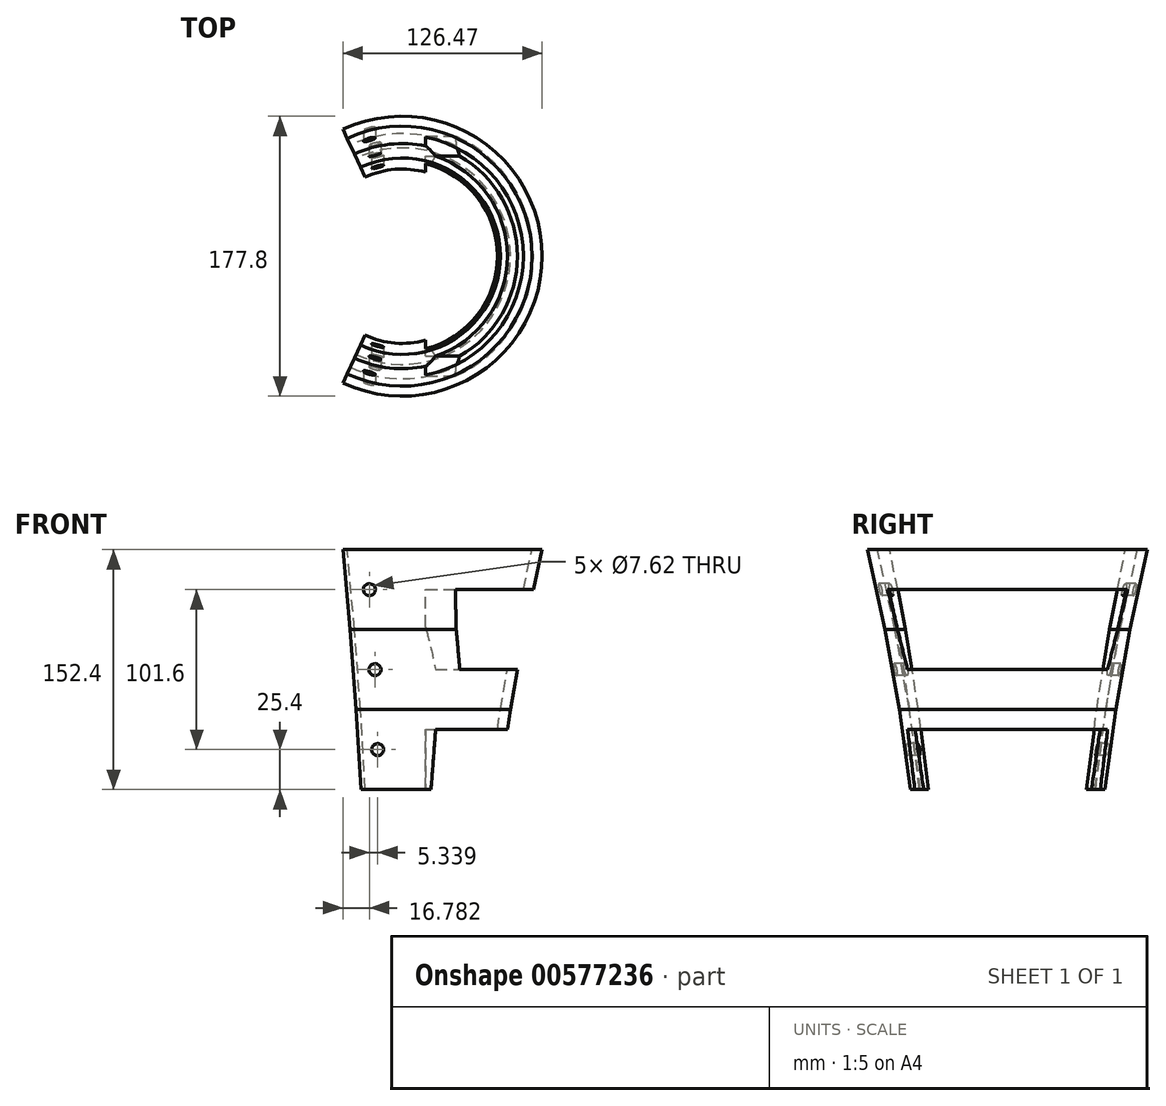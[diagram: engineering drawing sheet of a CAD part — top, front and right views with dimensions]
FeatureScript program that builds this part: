
annotation { "Feature Type Name" : "Feature", "Feature Type Description" : "" }
export const myFeature = defineFeature(function(context is Context, id is Id, definition is map)
    precondition{}
    {
        {
            var Q0;
            Q0=qCreatedBy(makeId("Front.planeOp"),FACE);
            var sketch = newSketch(context, id + "F0", { "sketchPlane" : qUnion([Q0])});
            skLineSegment(sketch, "E0", {"start": v(0, 0) * mm, "end": v(0, 50.8) * mm});
            skLineSegment(sketch, "E1", {"start": v(0, 50.8) * mm, "end": v(68.76, 50.8) * mm, "construction": true});
            skLineSegment(sketch, "E2", {"start": v(0, 0) * mm, "end": v(61.72, 0) * mm});
            skLineSegment(sketch, "E3", {"start": v(61.72, 0) * mm, "end": v(68.76, 50.8) * mm});
            skLineSegment(sketch, "E4", {"start": v(0, 50.8) * mm, "end": v(0, 101.6) * mm});
            skLineSegment(sketch, "E5", {"start": v(0, 101.6) * mm, "end": v(77.84, 101.6) * mm, "construction": true});
            skLineSegment(sketch, "E6", {"start": v(77.84, 101.6) * mm, "end": v(68.76, 50.8) * mm});
            skLineSegment(sketch, "E7", {"start": v(0, 101.6) * mm, "end": v(0, 152.4) * mm});
            skLineSegment(sketch, "E8", {"start": v(0, 152.4) * mm, "end": v(88.9, 152.4) * mm});
            skLineSegment(sketch, "E9", {"start": v(88.9, 152.4) * mm, "end": v(77.84, 101.6) * mm});
            skSolve(sketch);
        }
        {
            var Q0;
            Q0=qSketchRegion(id+"F0",true);
            var Q1;
            Q1=sQuery(id+"F0.wireOp",EDGE,"E7");
            revolve(context, id + "F1", {"entities" : qUnion([Q0]), "axis" : qUnion([Q1]), "revolveType" : RevolveType.SYMMETRIC, "angle" : 230 * degree});
        }
        {
            var Q0;
            Q0=qCreatedBy(makeId("Front.planeOp"),FACE);
            var sketch = newSketch(context, id + "F2", { "sketchPlane" : qUnion([Q0])});
            skLineSegment(sketch, "E10", {"start": v(0, 50.8) * mm, "end": v(62.4, 50.8) * mm, "construction": true});
            skLineSegment(sketch, "E11", {"start": v(0, 50.8) * mm, "end": v(0, 101.6) * mm});
            skLineSegment(sketch, "E12", {"start": v(0, 101.6) * mm, "end": v(71.49, 101.6) * mm, "construction": true});
            skLineSegment(sketch, "E13", {"start": v(71.49, 101.6) * mm, "end": v(62.4, 50.8) * mm});
            skLineSegment(sketch, "E14", {"start": v(0, 101.6) * mm, "end": v(0, 152.4) * mm});
            skLineSegment(sketch, "E15", {"start": v(0, 152.4) * mm, "end": v(82.55, 152.4) * mm});
            skLineSegment(sketch, "E16", {"start": v(82.55, 152.4) * mm, "end": v(71.49, 101.6) * mm});
            skPoint(sketch, "E17.start.orphan", {"position": v(1.44, 0) * mm});
            skLineSegment(sketch, "E18", {"start": v(0, 50.8) * mm, "end": v(0, 0) * mm});
            skLineSegment(sketch, "E19", {"start": v(0, 0) * mm, "end": v(55.37, 0) * mm});
            skLineSegment(sketch, "E20", {"start": v(55.37, 0) * mm, "end": v(62.4, 50.8) * mm});
            skSolve(sketch);
        }
        {
            var Q0;
            Q0=makeQuery(id+"F0.imprint","IMPRINT",FACE,{"disambiguationData":[TD([[makeQuery(id+"F0.imprint","IMPRINT",EDGE,{"derivedFrom":sQuery(id+"F0.wireOp",EDGE,"E0")}),-1.0]])]});
            var Q1;
            Q1=sQuery(id+"F2.wireOp",EDGE,"E11");
            revolve(context, id + "F3", {"operationType" : NewBodyOperationType.ADD, "entities" : qUnion([Q0]), "axis" : qUnion([Q1]), "revolveType" : RevolveType.ONE_DIRECTION, "oppositeDirection" : true, "angle" : 30 * degree});
        }
        {
            var Q0;
            Q0=qSketchRegion(id+"F2",true);
            var Q1;
            Q1=sQuery(id+"F2.wireOp",EDGE,"E14");
            revolve(context, id + "F4", {"operationType" : NewBodyOperationType.REMOVE, "entities" : qUnion([Q0]), "axis" : qUnion([Q1]), "revolveType" : RevolveType.FULL, "oppositeDirection" : true});
        }
        {
            var Q0;
            Q0=qCreatedBy(makeId("Front.planeOp"),FACE);
            var sketch = newSketch(context, id + "F5", { "sketchPlane" : qUnion([Q0])});
            skLineSegment(sketch, "E21", {"start": v(0, 0) * mm, "end": v(0, 50.8) * mm, "construction": true});
            skLineSegment(sketch, "E22", {"start": v(0, 50.8) * mm, "end": v(0, 101.6) * mm, "construction": true});
            skLineSegment(sketch, "E23", {"start": v(0, 101.6) * mm, "end": v(0, 152.4) * mm, "construction": true});
            skLineSegment(sketch, "E24", {"start": v(0, 127) * mm, "end": v(-20.79, 127) * mm, "construction": true});
            skPoint(sketch, "E24.endSnap0", {"position": v(0, 127) * mm});
            skLineSegment(sketch, "E25", {"start": v(0, 50.8) * mm, "end": v(0, 76.2) * mm, "construction": true});
            skLineSegment(sketch, "E26", {"start": v(0, 76.2) * mm, "end": v(-17.23, 76.2) * mm, "construction": true});
            skLineSegment(sketch, "E27", {"start": v(0, 0) * mm, "end": v(0, 25.4) * mm, "construction": true});
            skLineSegment(sketch, "E28", {"start": v(0, 25.4) * mm, "end": v(-15.45, 25.4) * mm, "construction": true});
            skCircle(sketch, "E29", {"center": v(-20.79, 127) * mm, "radius": 3.81 * mm});
            skCircle(sketch, "E30", {"center": v(-17.23, 76.2) * mm, "radius": 3.81 * mm});
            skCircle(sketch, "E31", {"center": v(-15.45, 25.4) * mm, "radius": 3.81 * mm});
            skSolve(sketch);
        }
        {
            var Q0;
            Q0 = qSketchRegion(id + "F5", true);
            extrude(context, id + "F6", {"entities" : qUnion([Q0]), "operationType" : NewBodyOperationType.REMOVE, "endBound" : BoundingType.SYMMETRIC, "oppositeDirection" : true, "depth" : 249.43 * mm, "offsetDistance" : 25.4 * mm});
        }
        {
            var Q0;
            Q0=qCreatedBy(makeId("Right.planeOp"),FACE);
            cPlane(context, id + "F7", {"entities" : qUnion([Q0]), "cplaneType" : CPlaneType.OFFSET, "offset" : 129.29 * mm, "width" : 152.4 * mm, "height" : 152.4 * mm});
        }
        {
            var Q0;
            Q0=qCreatedBy(id+"F7.planeOp",FACE);
            var sketch = newSketch(context, id + "F8", { "sketchPlane" : qUnion([Q0])});
            skLineSegment(sketch, "E32", {"start": v(0, 0) * mm, "end": v(55.88, 0) * mm});
            skLineSegment(sketch, "E33", {"start": v(0, 0) * mm, "end": v(-55.88, 0) * mm});
            skLineSegment(sketch, "E34", {"start": v(-55.88, 0) * mm, "end": v(-55.88, 38.1) * mm, "construction": true});
            skLineSegment(sketch, "E35", {"start": v(55.88, 0) * mm, "end": v(55.88, 38.1) * mm, "construction": true});
            skLineSegment(sketch, "E36", {"start": v(55.88, 38.1) * mm, "end": v(63.5, 38.1) * mm, "construction": true});
            skLineSegment(sketch, "E37", {"start": v(-55.88, 38.1) * mm, "end": v(-63.5, 38.1) * mm, "construction": true});
            skLineSegment(sketch, "E38", {"start": v(-63.5, 38.1) * mm, "end": v(63.5, 38.1) * mm});
            skLineSegment(sketch, "E39", {"start": v(55.88, 38.1) * mm, "end": v(55.88, 76.2) * mm, "construction": true});
            skLineSegment(sketch, "E40", {"start": v(55.88, 76.2) * mm, "end": v(55.88, 127) * mm, "construction": true});
            skLineSegment(sketch, "E41", {"start": v(-55.88, 38.1) * mm, "end": v(-55.88, 76.2) * mm, "construction": true});
            skLineSegment(sketch, "E42", {"start": v(-55.88, 76.2) * mm, "end": v(-55.88, 127) * mm, "construction": true});
            skLineSegment(sketch, "E43", {"start": v(-55.88, 127) * mm, "end": v(55.88, 127) * mm});
            skLineSegment(sketch, "E44", {"start": v(55.88, 127) * mm, "end": v(76.2, 127) * mm});
            skLineSegment(sketch, "E45", {"start": v(-55.88, 127) * mm, "end": v(-76.2, 127) * mm});
            skLineSegment(sketch, "E46", {"start": v(-55.88, 76.2) * mm, "end": v(55.88, 76.2) * mm});
            skLineSegment(sketch, "E47", {"start": v(-55.88, 76.2) * mm, "end": v(-63.5, 76.2) * mm});
            skLineSegment(sketch, "E48", {"start": v(55.88, 76.2) * mm, "end": v(63.5, 76.2) * mm});
            skLineSegment(sketch, "E49", {"start": v(63.5, 76.2) * mm, "end": v(76.2, 127) * mm});
            skLineSegment(sketch, "E50", {"start": v(-63.5, 76.2) * mm, "end": v(-76.2, 127) * mm});
            skLineSegment(sketch, "E51", {"start": v(-55.88, 0) * mm, "end": v(-58.93, 0) * mm});
            skLineSegment(sketch, "E52", {"start": v(-63.5, 38.1) * mm, "end": v(-58.93, 0) * mm});
            skLineSegment(sketch, "E53", {"start": v(55.88, 0) * mm, "end": v(58.93, 0) * mm});
            skLineSegment(sketch, "E54", {"start": v(58.93, 0) * mm, "end": v(63.5, 38.1) * mm});
            skSolve(sketch);
        }
        {
            var Q0;
            Q0 = qSketchRegion(id + "F8", true);
            extrude(context, id + "F9", {"entities" : qUnion([Q0]), "operationType" : NewBodyOperationType.REMOVE, "oppositeDirection" : true, "depth" : 114.3 * mm, "offsetDistance" : 25.4 * mm});
        }
    });
